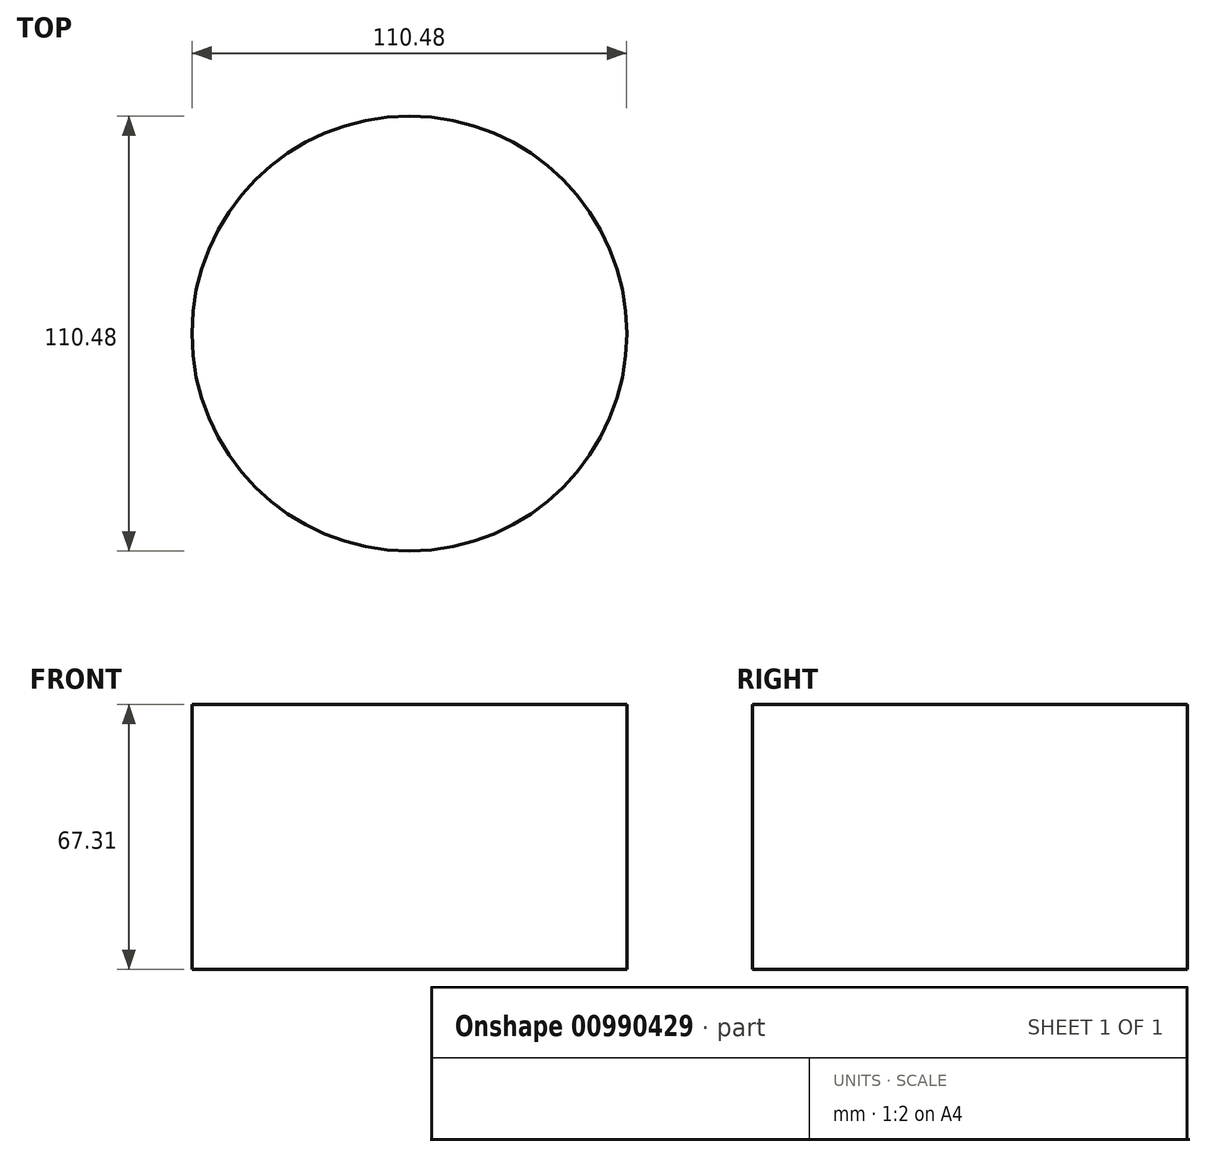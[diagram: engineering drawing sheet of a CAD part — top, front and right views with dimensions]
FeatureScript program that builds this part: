
annotation { "Feature Type Name" : "Feature", "Feature Type Description" : "" }
export const myFeature = defineFeature(function(context is Context, id is Id, definition is map)
    precondition{}
    {
        {
            var Q0;
            Q0=qCreatedBy(makeId("Top.planeOp"),FACE);
            var sketch = newSketch(context, id + "F0", { "sketchPlane" : qUnion([Q0])});
            skCircle(sketch, "E0", {"center": v(0, 0) * mm, "radius": 55.24 * mm});
            skSolve(sketch);
        }
        {
            var Q0;
            Q0 = qSketchRegion(id + "F0", true);
            extrude(context, id + "F1", {"entities" : qUnion([Q0]), "depth" : 67.3 * mm, "offsetDistance" : 25.4 * mm});
        }
    });
